# Revit family: APEX-400SP-50701-TR
name_source: partatom
category: Lighting Fixtures
units: mm (PartAtom-declared; Revit-internal decimal feet)

## family parameters
Cut with Voids When Loaded = Yes
Host = Face
Light Source = Yes
Maintain Annotation Orientation = No
Part Type = Normal
Room Calculation Point = No
Round Connector Dimension = Use Diameter
Shared = No

## types (6) — shared parameters
CRI = 70
Color Filter = 16777215
Default Elevation = 0' - 0"
Dimming Lamp Color Temperature Shift = <None>
IK Rating = IK08
IP Rating = IP66
Input Voltage = 120-277V
Lamp = LED
Load Classification = Lighting
Manufacturer = Above All Lighting
Power Factor = 0.9
Tilt Angle = 90.00°
URL = https://www.abovealllighting.com
Wattage Comments = 400W

## per-type parameters (varying)
| type | Beam Angle | Model | Photometric Web File |
| APEX-400SP-400W-5000K-12D | 12.00° | APEX-400SP-50701-TR-12-GY | APEX-400SP-400W-5000K-CRI70-12D.IES |
| APEX-400SP-400W-5000K-17D | 17.00° | APEX-400SP-50701-TR-17-GY | APEX-400SP-400W-5000K-CRI70-17D.IES |
| APEX-400SP-400W-5000K-22D | 22.00° | APEX-400SP-50701-TR-22-GY | APEX-400SP-400W-5000K-CRI70-22D.IES |
| APEX-400SP-400W-5000K-30D | 30.00° | APEX-400SP-50701-TR-30-GY | APEX-400SP-400W-5000K-CRI70-30D.IES |
| APEX-400SP-400W-5000K-45D | 45.00° | APEX-400SP-50701-TR-45-GY | APEX-400SP-400W-5000K-CRI70-45D.IES |
| APEX-400SP-400W-5000K-60D | 60.00° | APEX-400SP-50701-TR-60-GY | APEX-400SP-400W-5000K-CRI70-60D.IES |

## geometry (parser evidence)
native form markers: Sweep x3
no freeform markers — native parametric forms only
